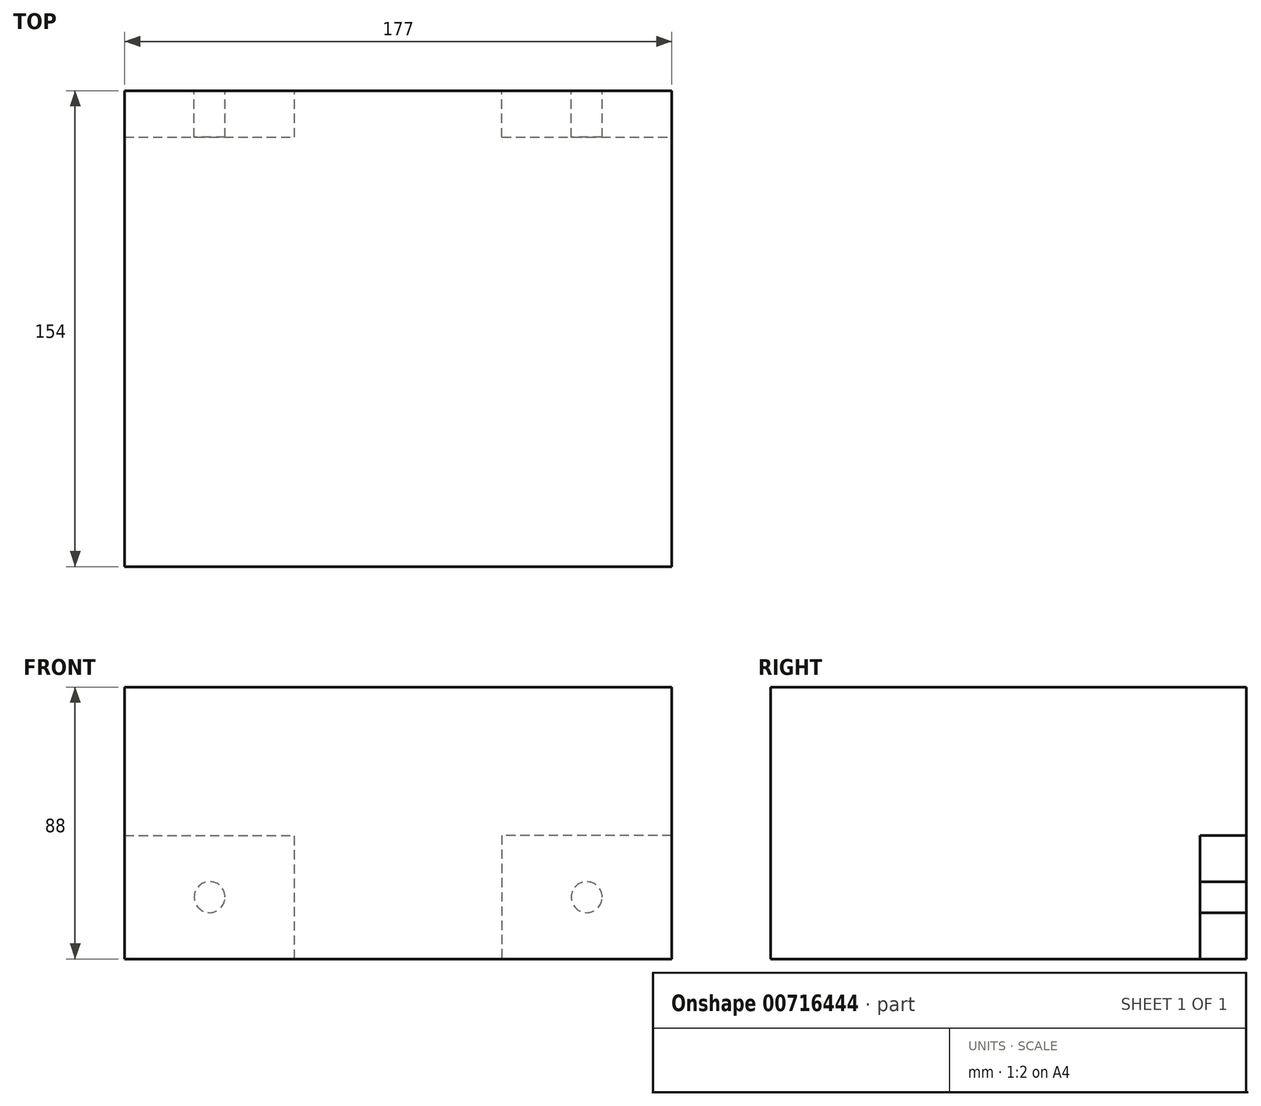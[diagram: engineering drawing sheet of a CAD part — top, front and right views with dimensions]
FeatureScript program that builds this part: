
annotation { "Feature Type Name" : "Feature", "Feature Type Description" : "" }
export const myFeature = defineFeature(function(context is Context, id is Id, definition is map)
    precondition{}
    {
        {
            var Q0;
            Q0=qCreatedBy(makeId("Top.planeOp"),FACE);
            var sketch = newSketch(context, id + "F0", { "sketchPlane" : qUnion([Q0])});
            skLineSegment(sketch, "E0.bottom", {"start": v(0, 0) * mm, "end": v(177, 0) * mm});
            skLineSegment(sketch, "E0.top", {"start": v(0, 154) * mm, "end": v(177, 154) * mm});
            skLineSegment(sketch, "E0.left", {"start": v(0, 0) * mm, "end": v(0, 154) * mm});
            skLineSegment(sketch, "E0.right", {"start": v(177, 0) * mm, "end": v(177, 154) * mm});
            skSolve(sketch);
        }
        {
            var Q0;
            Q0 = qSketchRegion(id + "F0", true);
            extrude(context, id + "F1", {"entities" : qUnion([Q0]), "depth" : 88 * mm, "offsetDistance" : 25 * mm});
        }
        {
            var Q0;
            Q0=makeQuery(id+"F1.opExtrude","SWEPT_FACE",FACE,{"disambiguationData":[OSD([sQuery(id+"F0.wireOp",EDGE,"E0.top")])]});
            var sketch = newSketch(context, id + "F2", { "sketchPlane" : qUnion([Q0])});
            skLineSegment(sketch, "E1.bottom", {"start": v(-177, 40) * mm, "end": v(-122, 40) * mm});
            skLineSegment(sketch, "E1.top", {"start": v(-177, 0) * mm, "end": v(-122, 0) * mm});
            skLineSegment(sketch, "E1.left", {"start": v(-177, 40) * mm, "end": v(-177, 0) * mm});
            skLineSegment(sketch, "E1.right", {"start": v(-122, 40) * mm, "end": v(-122, 0) * mm});
            skLineSegment(sketch, "E2.bottom", {"start": v(0, 0) * mm, "end": v(-55, 0) * mm});
            skLineSegment(sketch, "E2.top", {"start": v(0, 40) * mm, "end": v(-55, 40) * mm});
            skLineSegment(sketch, "E2.left", {"start": v(0, 0) * mm, "end": v(0, 40) * mm});
            skLineSegment(sketch, "E2.right", {"start": v(-55, 0) * mm, "end": v(-55, 40) * mm});
            skCircle(sketch, "E3", {"center": v(-149.5, 20) * mm, "radius": 5 * mm});
            skPoint(sketch, "E3.centerSnap0", {"position": v(-177, 20) * mm});
            skPoint(sketch, "E3.centerSnap1", {"position": v(-149.5, 40) * mm});
            skCircle(sketch, "E4", {"center": v(-27.5, 20) * mm, "radius": 5 * mm});
            skPoint(sketch, "E4.centerSnap0", {"position": v(-55, 20) * mm});
            skPoint(sketch, "E4.centerSnap1", {"position": v(-27.5, 40) * mm});
            skSolve(sketch);
        }
        {
            var Q0;
            Q0 = qSketchRegion(id + "F2", true);
            extrude(context, id + "F3", {"entities" : qUnion([Q0]), "operationType" : NewBodyOperationType.REMOVE, "oppositeDirection" : true, "depth" : 15 * mm, "offsetDistance" : 25 * mm});
        }
    });
